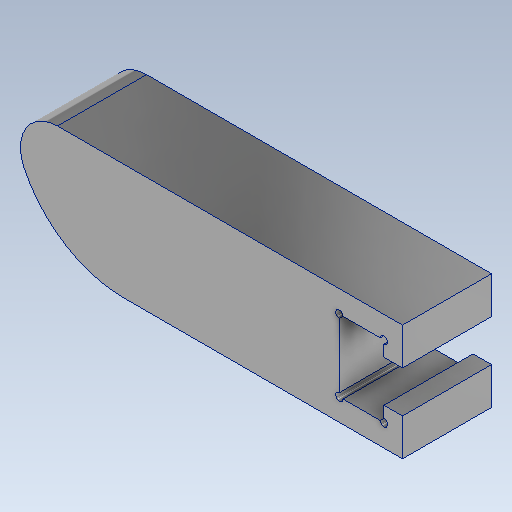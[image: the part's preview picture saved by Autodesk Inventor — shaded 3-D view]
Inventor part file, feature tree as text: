
AUTODESK INVENTOR PART (.ipt)
format: ipt  version: 2025.2 (Build 292293000, 293)  size: 442,368 bytes
history: native  units: mm
features: extrude x2, fillet x2, sketch x1
ambient origin geometry x8: Origin, YZ Plane, XZ Plane, XY Plane, X Axis, Y Axis, Z Axis, Center Point
bodies: Solid2 (feature_tree)
feature tree (5):
  extrude  "Extrusion2"  Depth=5.0mm
  fillet  "Fillet2"  Radius=2.5mm
  extrude  "Extrusion7"  Depth=12.0mm TaperAngle=0.0deg
  fillet  "Rundung3"  Radius=44.7mm
  sketch  "Sketch11"  dims[d41=6.0mm d48=44.0mm d50=2.5mm d56=12.0mm d57=0.0mm d63=44.7mm d67=15.6mm d71=0.0mm d87=5.6mm d88=9.65mm d97=15.6mm d98=15.0mm d99=1.0mm d100=1.0mm d101=1.0mm d102=1.0mm d103=0.0mm d104=0.0mm d105=5.0mm]
